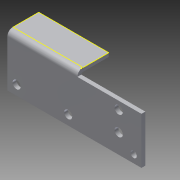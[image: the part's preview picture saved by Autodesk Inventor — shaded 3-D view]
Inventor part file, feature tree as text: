
AUTODESK INVENTOR PART (.ipt)
format: ipt  version: 2013 (Build 170138000, 138)  size: 195,072 bytes
history: native  units: in
note: dims shown in document units (in); Inventor stores cm internally (conversion verified against a paired STEP export)
features: sketch x7, other x6, sheet_metal_op x4, reference x4, extrude x1
ambient origin geometry x8: Origin, YZ Plane, XZ Plane, XY Plane, X Axis, Y Axis, Z Axis, Center Point
bodies: Solid1 (feature_tree)
feature tree (22):
  sheet_metal_op  "Face1"
  sheet_metal_op  "Flange1"
  sketch  "Sketch9"  dims[d5=0.295in]
  extrude  "Extrusion1"  Depth=1.5in
  sketch  "Sketch1"  dims[d1=2.244in d2=1.5in]
  other  "Plate1"
  sketch  "Sketch2"  dims[d3=0.295in]
  other  "Plate2"
  sheet_metal_op  "Bend1"
  sheet_metal_op  "Corner1"
  sketch  "Sketch8"  dims[d4=1.181in]
  reference  "Reference1"
  reference  "Reference2"
  sketch  "Sketch10"  dims[d8=0.125in]
  sketch  "Sketch12"  dims[d9=0.125in]
  reference  "Reference5"
  reference  "Reference6"
  sketch  "Sketch13"  dims[d10=0.0625in d11=0.25in d12=0.125in d13=1.0in d14=90.0deg d15=0.05in d16=0.5in d17=0.125in d18=0.125in d19=0.125in d20=0.0in d21=2.053in d22=0.0in d25=0.125in d26=0.0in d27=0.25in d28=0.25in d29=0.2in d30=0.125in d31=0.0in d0=0.0625in d6=0.0in]
  other  "Cut1"
  other  "Cut3"
  other  "Cut4"
  other  "Definition1"
